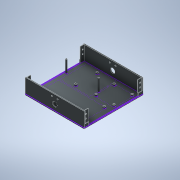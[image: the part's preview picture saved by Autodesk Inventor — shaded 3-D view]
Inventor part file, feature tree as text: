
AUTODESK INVENTOR PART (.ipt)
format: ipt  version: 2022 (Build 260153000, 153)  size: 347,648 bytes
history: native  units: in
note: dims shown in document units (in); Inventor stores cm internally (conversion verified against a paired STEP export)
features: extrude x18, sketch x7
ambient origin geometry x8: Origin, YZ Plane, XZ Plane, XY Plane, X Axis, Y Axis, Z Axis, Center Point
bodies: Solid1 (feature_tree)
feature tree (25):
  sketch  "Sketch1"  dims[d0=4.7244in d1=4.7244in]
  extrude  "Extrusion1"  Depth=4.7244in
  extrude  "Extrusion2"  Depth=2.1181in
  extrude  "Extrusion3"  Depth=2.248in
  extrude  "Extrusion4"  Depth=1.7047in
  extrude  "Extrusion5"  Depth=0.4182in
  extrude  "Extrusion6"  Depth=0.134in
  extrude  "Extrusion7"  Depth=0.0591in
  extrude  "Extrusion8"  Depth=0.0591in
  extrude  "Extrusion9"  Depth=0.0591in
  extrude  "Extrusion10"  Depth=0.0591in
  extrude  "Extrusion11"  Depth=0.0591in
  extrude  "Extrusion12"  Depth=0.0591in
  extrude  "Extrusion13"  Depth=0.0591in
  extrude  "Extrusion14"  Depth=0.0591in
  extrude  "Extrusion15"  Depth=0.0394in
  extrude  "Extrusion16"  Depth=0.0394in
  extrude  "Extrusion17"  Depth=0.0394in
  extrude  "Extrusion18"  Depth=0.0394in
  sketch  "Sketch3"  dims[d8=3.9961in d9=2.1181in]
  sketch  "Sketch4"  dims[d10=2.4646in d11=2.248in]
  sketch  "Sketch5"  dims[d12=1.7047in d13=1.7047in]
  sketch  "Sketch6"  dims[d24=0.1601in d25=0.4182in]
  sketch  "Sketch7"  dims[d27=0.4018in d28=0.134in]
  sketch  "Sketch8"  dims[d29=0.0935in d30=0.3188in d39=0.1102in d40=0.1102in d41=0.2402in d42=0.1102in d43=0.1102in d44=0.1102in d45=0.1102in d46=0.0394in d47=0.0394in d48=0.0394in d49=0.0394in d50=0.1102in d51=0.1102in d52=0.1102in d53=0.1102in d54=0.1102in d55=0.1102in d56=0.1102in d57=0.1102in d58=0.0551in d59=0.0433in d60=0.0551in d61=0.0433in d62=0.0433in d63=0.0551in d64=0.0433in d65=0.0551in d66=0.189in d67=0.189in d68=0.189in d69=0.189in d70=0.189in d71=0.189in d72=0.189in d73=0.189in d74=4.8819in d75=4.8819in d76=0.0787in d77=0.0787in d78=0.0984in d79=0.0in d80=1.1811in d81=0.0in d82=0.1181in d83=0.0in d84=0.1181in d85=0.0in d86=0.1181in d87=0.0in d88=0.1181in d89=0.0in d90=0.1181in d91=0.0in d92=0.1181in d93=0.0in d94=0.1181in d95=0.0in d96=0.1181in d97=0.0in d98=4.0945in d99=0.3937in d100=0.1181in d101=0.0in d102=4.0945in d103=0.3937in d104=0.1181in d105=0.0in d106=0.1102in d107=0.1102in d108=0.1102in d109=0.1102in d110=0.1378in d111=0.1378in d112=0.3346in d115=0.3031in d120=0.3031in d121=0.3346in d122=0.1102in d123=0.1102in d124=0.1929in d125=0.1929in d126=0.1929in d127=0.1929in d128=5.1181in d129=0.0in d130=0.3937in d131=0.3937in d132=0.5118in d133=0.1102in d134=0.1102in d135=0.1102in d136=0.1102in d137=0.3661in d138=0.2244in d139=2.1476in d140=2.1476in d141=2.2441in d142=5.1181in d143=0.0in d144=1.7323in d145=0.1102in d146=1.6142in d148=0.1102in d149=0.1102in d150=1.9685in d152=1.0236in d153=0.0in d154=0.1102in d155=1.9685in d156=0.9449in d157=0.9449in d158=0.0394in d159=0.0in d160=0.9449in d161=0.9449in d162=0.0394in d163=0.0in d164=0.0591in d165=0.0in]
